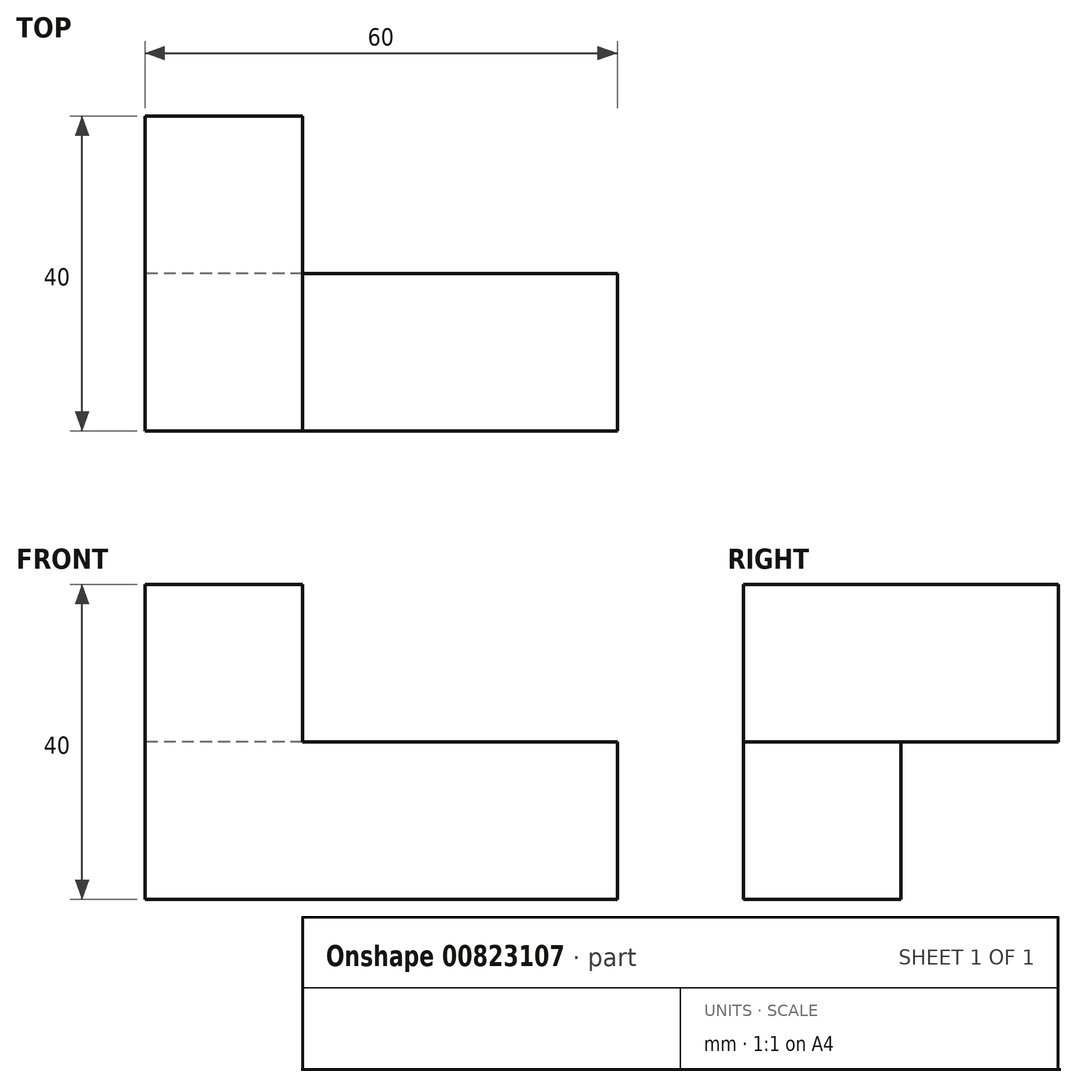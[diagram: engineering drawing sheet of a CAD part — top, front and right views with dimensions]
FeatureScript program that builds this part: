
annotation { "Feature Type Name" : "Feature", "Feature Type Description" : "" }
export const myFeature = defineFeature(function(context is Context, id is Id, definition is map)
    precondition{}
    {
        {
            var Q0;
            Q0=qCreatedBy(makeId("Front.planeOp"),FACE);
            var sketch = newSketch(context, id + "F0", { "sketchPlane" : qUnion([Q0])});
            skLineSegment(sketch, "E0.bottom", {"start": v(0, 0) * mm, "end": v(20, 0) * mm});
            skLineSegment(sketch, "E0.top", {"start": v(0, 20) * mm, "end": v(20, 20) * mm});
            skLineSegment(sketch, "E0.left", {"start": v(0, 0) * mm, "end": v(0, 20) * mm});
            skLineSegment(sketch, "E0.right", {"start": v(20, 0) * mm, "end": v(20, 20) * mm});
            skSolve(sketch);
        }
        {
            var Q0;
            Q0 = qSketchRegion(id + "F0", true);
            extrude(context, id + "F1", {"entities" : qUnion([Q0]), "depth" : 40 * mm, "offsetDistance" : 25.4 * mm});
        }
        {
            var Q0;
            Q0=makeQuery(id+"F1.opExtrude","SWEPT_FACE",FACE,{"disambiguationData":[OSD([sQuery(id+"F0.wireOp",EDGE,"E0.bottom")])]});
            var sketch = newSketch(context, id + "F2", { "sketchPlane" : qUnion([Q0])});
            skLineSegment(sketch, "E1.bottom", {"start": v(20, 40) * mm, "end": v(0, 40) * mm});
            skLineSegment(sketch, "E1.top", {"start": v(20, 20) * mm, "end": v(0, 20) * mm});
            skLineSegment(sketch, "E1.left", {"start": v(20, 40) * mm, "end": v(20, 20) * mm});
            skLineSegment(sketch, "E1.right", {"start": v(0, 40) * mm, "end": v(0, 20) * mm});
            skSolve(sketch);
        }
        {
            var Q0;
            Q0=makeQuery(id+"F2.imprint","IMPRINT",FACE,{"disambiguationData":[TD([[makeQuery(id+"F2.imprint","IMPRINT",EDGE,{"derivedFrom":sQuery(id+"F2.wireOp",EDGE,"E1.bottom")}),-1.0]])]});
            extrude(context, id + "F3", {"entities" : qUnion([Q0]), "operationType" : NewBodyOperationType.ADD, "depth" : 20 * mm, "offsetDistance" : 25.4 * mm});
        }
        {
            var Q0;
            Q0=makeQuery(id+"F3.boolean.opBoolean","MERGE",FACE,{"derivedFrom":[makeQuery(id+"F1.opExtrude","SWEPT_FACE",FACE,{"disambiguationData":[OSD([sQuery(id+"F0.wireOp",EDGE,"E0.right")])]}),makeQuery(id+"F3.opExtrude","SWEPT_FACE",FACE,{"disambiguationData":[OSD([sQuery(id+"F2.wireOp",EDGE,"E1.left")])]})]});
            var sketch = newSketch(context, id + "F4", { "sketchPlane" : qUnion([Q0])});
            skLineSegment(sketch, "E2.bottom", {"start": v(-20, 0) * mm, "end": v(-40, 0) * mm});
            skLineSegment(sketch, "E2.top", {"start": v(-20, -20) * mm, "end": v(-40, -20) * mm});
            skLineSegment(sketch, "E2.left", {"start": v(-20, 0) * mm, "end": v(-20, -20) * mm});
            skLineSegment(sketch, "E2.right", {"start": v(-40, 0) * mm, "end": v(-40, -20) * mm});
            skSolve(sketch);
        }
        {
            var Q0;
            Q0=makeQuery(id+"F4.imprint","IMPRINT",FACE,{"disambiguationData":[TD([[makeQuery(id+"F4.imprint","IMPRINT",EDGE,{"derivedFrom":sQuery(id+"F4.wireOp",EDGE,"E2.bottom")}),1.0]])]});
            extrude(context, id + "F5", {"entities" : qUnion([Q0]), "operationType" : NewBodyOperationType.ADD, "depth" : 40 * mm, "offsetDistance" : 25.4 * mm});
        }
    });
